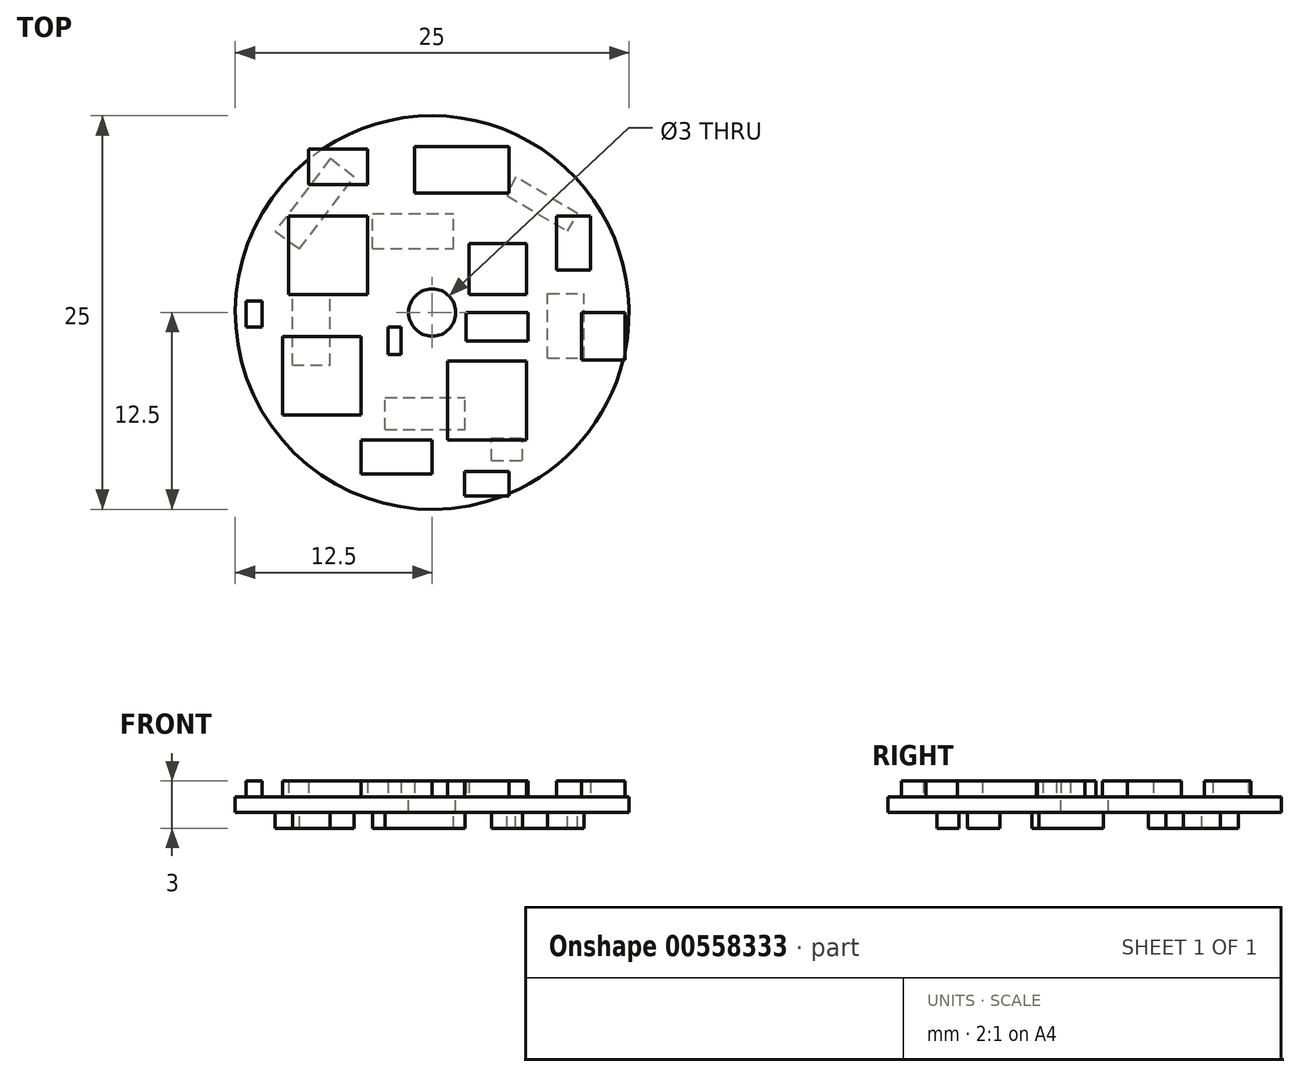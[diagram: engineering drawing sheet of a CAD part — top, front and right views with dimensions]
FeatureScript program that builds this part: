
annotation { "Feature Type Name" : "Feature", "Feature Type Description" : "" }
export const myFeature = defineFeature(function(context is Context, id is Id, definition is map)
    precondition{}
    {
        {
            var Q0;
            Q0=qCreatedBy(makeId("Top.planeOp"),FACE);
            var sketch = newSketch(context, id + "F0", { "sketchPlane" : qUnion([Q0])});
            skCircle(sketch, "E0", {"center": v(0, 0) * mm, "radius": 12.5 * mm});
            skSolve(sketch);
        }
        {
            var Q0;
            Q0 = qSketchRegion(id + "F0", true);
            extrude(context, id + "F1", {"entities" : qUnion([Q0]), "depth" : 1 * mm, "offsetDistance" : 25 * mm});
        }
        {
            var Q0;
            Q0=makeQuery(id+"F1.opExtrude","CAP_FACE",FACE,{"disambiguationData":[OSD([sQuery(id+"F0.wireOp",EDGE,"E0")])],"isStart":false});
            var sketch = newSketch(context, id + "F2", { "sketchPlane" : qUnion([Q0])});
            skLineSegment(sketch, "E1.bottom", {"start": v(-9.5, -1.51) * mm, "end": v(-4.5, -1.51) * mm});
            skLineSegment(sketch, "E1.top", {"start": v(-9.5, -6.51) * mm, "end": v(-4.5, -6.51) * mm});
            skLineSegment(sketch, "E1.left", {"start": v(-9.5, -1.51) * mm, "end": v(-9.5, -6.51) * mm});
            skLineSegment(sketch, "E1.right", {"start": v(-4.5, -1.51) * mm, "end": v(-4.5, -6.51) * mm});
            skLineSegment(sketch, "E2.bottom", {"start": v(0.99, -3.08) * mm, "end": v(5.99, -3.08) * mm});
            skLineSegment(sketch, "E2.top", {"start": v(0.99, -8.08) * mm, "end": v(5.99, -8.08) * mm});
            skLineSegment(sketch, "E2.left", {"start": v(0.99, -3.08) * mm, "end": v(0.99, -8.08) * mm});
            skLineSegment(sketch, "E2.right", {"start": v(5.99, -3.08) * mm, "end": v(5.99, -8.08) * mm});
            skLineSegment(sketch, "E3.bottom", {"start": v(-9.11, 6.13) * mm, "end": v(-4.11, 6.13) * mm});
            skLineSegment(sketch, "E3.top", {"start": v(-9.11, 1.13) * mm, "end": v(-4.11, 1.13) * mm});
            skLineSegment(sketch, "E3.left", {"start": v(-9.11, 6.13) * mm, "end": v(-9.11, 1.13) * mm});
            skLineSegment(sketch, "E3.right", {"start": v(-4.11, 6.13) * mm, "end": v(-4.11, 1.13) * mm});
            skLineSegment(sketch, "E4.bottom", {"start": v(2.36, 4.37) * mm, "end": v(5.99, 4.37) * mm});
            skLineSegment(sketch, "E4.top", {"start": v(2.36, 1.13) * mm, "end": v(5.99, 1.13) * mm});
            skLineSegment(sketch, "E4.left", {"start": v(2.36, 4.37) * mm, "end": v(2.36, 1.13) * mm});
            skLineSegment(sketch, "E4.right", {"start": v(5.99, 4.37) * mm, "end": v(5.99, 1.13) * mm});
            skLineSegment(sketch, "E5.bottom", {"start": v(-1.11, 10.54) * mm, "end": v(4.89, 10.54) * mm});
            skLineSegment(sketch, "E5.top", {"start": v(-1.11, 7.6) * mm, "end": v(4.89, 7.6) * mm});
            skLineSegment(sketch, "E5.left", {"start": v(-1.11, 10.54) * mm, "end": v(-1.11, 7.6) * mm});
            skLineSegment(sketch, "E5.right", {"start": v(4.89, 10.54) * mm, "end": v(4.89, 7.6) * mm});
            skLineSegment(sketch, "E6.bottom", {"start": v(9.5, 0) * mm, "end": v(12.25, 0) * mm});
            skLineSegment(sketch, "E6.top", {"start": v(9.5, -3) * mm, "end": v(12.25, -3) * mm});
            skLineSegment(sketch, "E6.left", {"start": v(9.5, 0) * mm, "end": v(9.5, -3) * mm});
            skLineSegment(sketch, "E6.right", {"start": v(12.25, 0) * mm, "end": v(12.25, -3) * mm});
            skLineSegment(sketch, "E7.bottom", {"start": v(-7.84, 10.39) * mm, "end": v(-4.11, 10.39) * mm});
            skLineSegment(sketch, "E7.top", {"start": v(-7.84, 8.13) * mm, "end": v(-4.11, 8.13) * mm});
            skLineSegment(sketch, "E7.left", {"start": v(-7.84, 10.39) * mm, "end": v(-7.84, 8.13) * mm});
            skLineSegment(sketch, "E7.right", {"start": v(-4.11, 10.39) * mm, "end": v(-4.11, 8.13) * mm});
            skLineSegment(sketch, "E8.bottom", {"start": v(-4.5, -8.08) * mm, "end": v(0, -8.08) * mm});
            skLineSegment(sketch, "E8.top", {"start": v(-4.5, -10.24) * mm, "end": v(0, -10.24) * mm});
            skLineSegment(sketch, "E8.left", {"start": v(-4.5, -8.08) * mm, "end": v(-4.5, -10.24) * mm});
            skLineSegment(sketch, "E8.right", {"start": v(0, -8.08) * mm, "end": v(0, -10.24) * mm});
            skLineSegment(sketch, "E9.bottom", {"start": v(2.05, -10.08) * mm, "end": v(4.89, -10.08) * mm});
            skLineSegment(sketch, "E9.top", {"start": v(2.05, -11.65) * mm, "end": v(4.89, -11.65) * mm});
            skLineSegment(sketch, "E9.left", {"start": v(2.05, -10.08) * mm, "end": v(2.05, -11.65) * mm});
            skLineSegment(sketch, "E9.right", {"start": v(4.89, -10.08) * mm, "end": v(4.89, -11.65) * mm});
            skLineSegment(sketch, "E10.bottom", {"start": v(7.89, 6.13) * mm, "end": v(10.05, 6.13) * mm});
            skLineSegment(sketch, "E10.top", {"start": v(7.89, 2.7) * mm, "end": v(10.05, 2.7) * mm});
            skLineSegment(sketch, "E10.left", {"start": v(7.89, 6.13) * mm, "end": v(7.89, 2.7) * mm});
            skLineSegment(sketch, "E10.right", {"start": v(10.05, 6.13) * mm, "end": v(10.05, 2.7) * mm});
            skLineSegment(sketch, "E11.bottom", {"start": v(2.16, 0) * mm, "end": v(6.09, 0) * mm});
            skLineSegment(sketch, "E11.top", {"start": v(2.16, -1.8) * mm, "end": v(6.09, -1.8) * mm});
            skLineSegment(sketch, "E11.left", {"start": v(2.16, 0) * mm, "end": v(2.16, -1.8) * mm});
            skLineSegment(sketch, "E11.right", {"start": v(6.09, 0) * mm, "end": v(6.09, -1.8) * mm});
            skLineSegment(sketch, "E12.bottom", {"start": v(-11.81, 0.72) * mm, "end": v(-10.81, 0.72) * mm});
            skLineSegment(sketch, "E12.top", {"start": v(-11.81, -0.91) * mm, "end": v(-10.81, -0.91) * mm});
            skLineSegment(sketch, "E12.left", {"start": v(-11.81, 0.72) * mm, "end": v(-11.81, -0.91) * mm});
            skLineSegment(sketch, "E12.right", {"start": v(-10.81, 0.72) * mm, "end": v(-10.81, -0.91) * mm});
            skLineSegment(sketch, "E13.bottom", {"start": v(-2.8, -0.91) * mm, "end": v(-1.99, -0.91) * mm});
            skLineSegment(sketch, "E13.top", {"start": v(-2.8, -2.66) * mm, "end": v(-1.99, -2.66) * mm});
            skLineSegment(sketch, "E13.left", {"start": v(-2.8, -0.91) * mm, "end": v(-2.8, -2.66) * mm});
            skLineSegment(sketch, "E13.right", {"start": v(-1.99, -0.91) * mm, "end": v(-1.99, -2.66) * mm});
            skSolve(sketch);
        }
        {
            var Q0;
            Q0 = qSketchRegion(id + "F2", true);
            extrude(context, id + "F3", {"entities" : qUnion([Q0]), "operationType" : NewBodyOperationType.ADD, "depth" : 1 * mm, "offsetDistance" : 25 * mm});
        }
        {
            var Q0;
            Q0=makeQuery(id+"F1.opExtrude","CAP_FACE",FACE,{"disambiguationData":[OSD([sQuery(id+"F0.wireOp",EDGE,"E0")])],"isStart":true});
            var sketch = newSketch(context, id + "F4", { "sketchPlane" : qUnion([Q0])});
            skLineSegment(sketch, "E14.bottom", {"start": v(-8.87, 3.34) * mm, "end": v(-6.47, 3.34) * mm});
            skLineSegment(sketch, "E14.top", {"start": v(-8.87, -1.2) * mm, "end": v(-6.47, -1.2) * mm});
            skLineSegment(sketch, "E14.left", {"start": v(-8.87, 3.34) * mm, "end": v(-8.87, -1.2) * mm});
            skLineSegment(sketch, "E14.right", {"start": v(-6.47, 3.34) * mm, "end": v(-6.47, -1.2) * mm});
            skLineSegment(sketch, "E15.bottom", {"start": v(-3.8, -4.05) * mm, "end": v(1.37, -4.05) * mm});
            skLineSegment(sketch, "E15.top", {"start": v(-3.8, -6.28) * mm, "end": v(1.37, -6.28) * mm});
            skLineSegment(sketch, "E15.left", {"start": v(-3.8, -4.05) * mm, "end": v(-3.8, -6.28) * mm});
            skLineSegment(sketch, "E15.right", {"start": v(1.37, -4.05) * mm, "end": v(1.37, -6.28) * mm});
            skLineSegment(sketch, "E16.bottom", {"start": v(7.34, 2.9) * mm, "end": v(9.66, 2.9) * mm});
            skLineSegment(sketch, "E16.top", {"start": v(7.34, -1.2) * mm, "end": v(9.66, -1.2) * mm});
            skLineSegment(sketch, "E16.left", {"start": v(7.34, 2.9) * mm, "end": v(7.34, -1.2) * mm});
            skLineSegment(sketch, "E16.right", {"start": v(9.66, 2.9) * mm, "end": v(9.66, -1.2) * mm});
            skLineSegment(sketch, "E17.bottom", {"start": v(-3, 7.44) * mm, "end": v(2.08, 7.44) * mm});
            skLineSegment(sketch, "E17.top", {"start": v(-3, 5.4) * mm, "end": v(2.08, 5.4) * mm});
            skLineSegment(sketch, "E17.left", {"start": v(-3, 7.44) * mm, "end": v(-3, 5.4) * mm});
            skLineSegment(sketch, "E17.right", {"start": v(2.08, 7.44) * mm, "end": v(2.08, 5.4) * mm});
            skLineSegment(sketch, "E18.bottom", {"start": v(3.78, 9.4) * mm, "end": v(5.74, 9.4) * mm});
            skLineSegment(sketch, "E18.top", {"start": v(3.78, 7.98) * mm, "end": v(5.74, 7.98) * mm});
            skLineSegment(sketch, "E18.left", {"start": v(3.78, 9.4) * mm, "end": v(3.78, 7.98) * mm});
            skLineSegment(sketch, "E18.right", {"start": v(5.74, 9.4) * mm, "end": v(5.74, 7.98) * mm});
            skLineSegment(sketch, "E19", {"start": v(4.76, -7.43) * mm, "end": v(8.59, -5.16) * mm});
            skPoint(sketch, "E19.endSnap0", {"position": v(-3.8, -5.16) * mm});
            skLineSegment(sketch, "E20", {"start": v(8.59, -5.16) * mm, "end": v(9.25, -6.28) * mm});
            skLineSegment(sketch, "E21", {"start": v(9.25, -6.28) * mm, "end": v(5.3, -8.61) * mm});
            skLineSegment(sketch, "E22", {"start": v(5.3, -8.61) * mm, "end": v(4.76, -7.43) * mm});
            skLineSegment(sketch, "E23", {"start": v(-8.43, -4.05) * mm, "end": v(-4.95, -8.61) * mm});
            skLineSegment(sketch, "E24", {"start": v(-4.95, -8.61) * mm, "end": v(-6.47, -9.77) * mm});
            skLineSegment(sketch, "E25", {"start": v(-6.47, -9.77) * mm, "end": v(-9.97, -5.16) * mm});
            skLineSegment(sketch, "E26", {"start": v(-9.97, -5.16) * mm, "end": v(-8.43, -4.05) * mm});
            skSolve(sketch);
        }
        {
            var Q0;
            Q0 = qSketchRegion(id + "F4", true);
            extrude(context, id + "F5", {"entities" : qUnion([Q0]), "operationType" : NewBodyOperationType.ADD, "depth" : 1 * mm, "offsetDistance" : 25 * mm});
        }
        {
            var Q0;
            Q0=makeQuery(id+"F1.opExtrude","CAP_FACE",FACE,{"disambiguationData":[OSD([sQuery(id+"F0.wireOp",EDGE,"E0")])],"isStart":false});
            var sketch = newSketch(context, id + "F6", { "sketchPlane" : qUnion([Q0])});
            skCircle(sketch, "E27", {"center": v(0, 0) * mm, "radius": 1 * mm});
            skSolve(sketch);
        }
        {
            var Q0;
            Q0=sQuery(id+"F6.wireOp",VERTEX,"E27.center");
            var Q1;
            Q1=makeQuery(id+"F1.opExtrude","SWEPT_BODY",BODY,{"disambiguationData":[OSD([sQuery(id+"F0.wireOp",EDGE,"E0")])]});
            hole(context, id + "F7", {"style" : HoleStyle.SIMPLE, "endStyle" : HoleEndStyle.THROUGH, "holeDiameter" : 3 * mm, "isTappedThrough" : true, "tappedDepth" : 12 * mm, "tapClearance" : 3, "locations" : qUnion([Q0]), "scope" : qUnion([Q1])});
        }
    });
